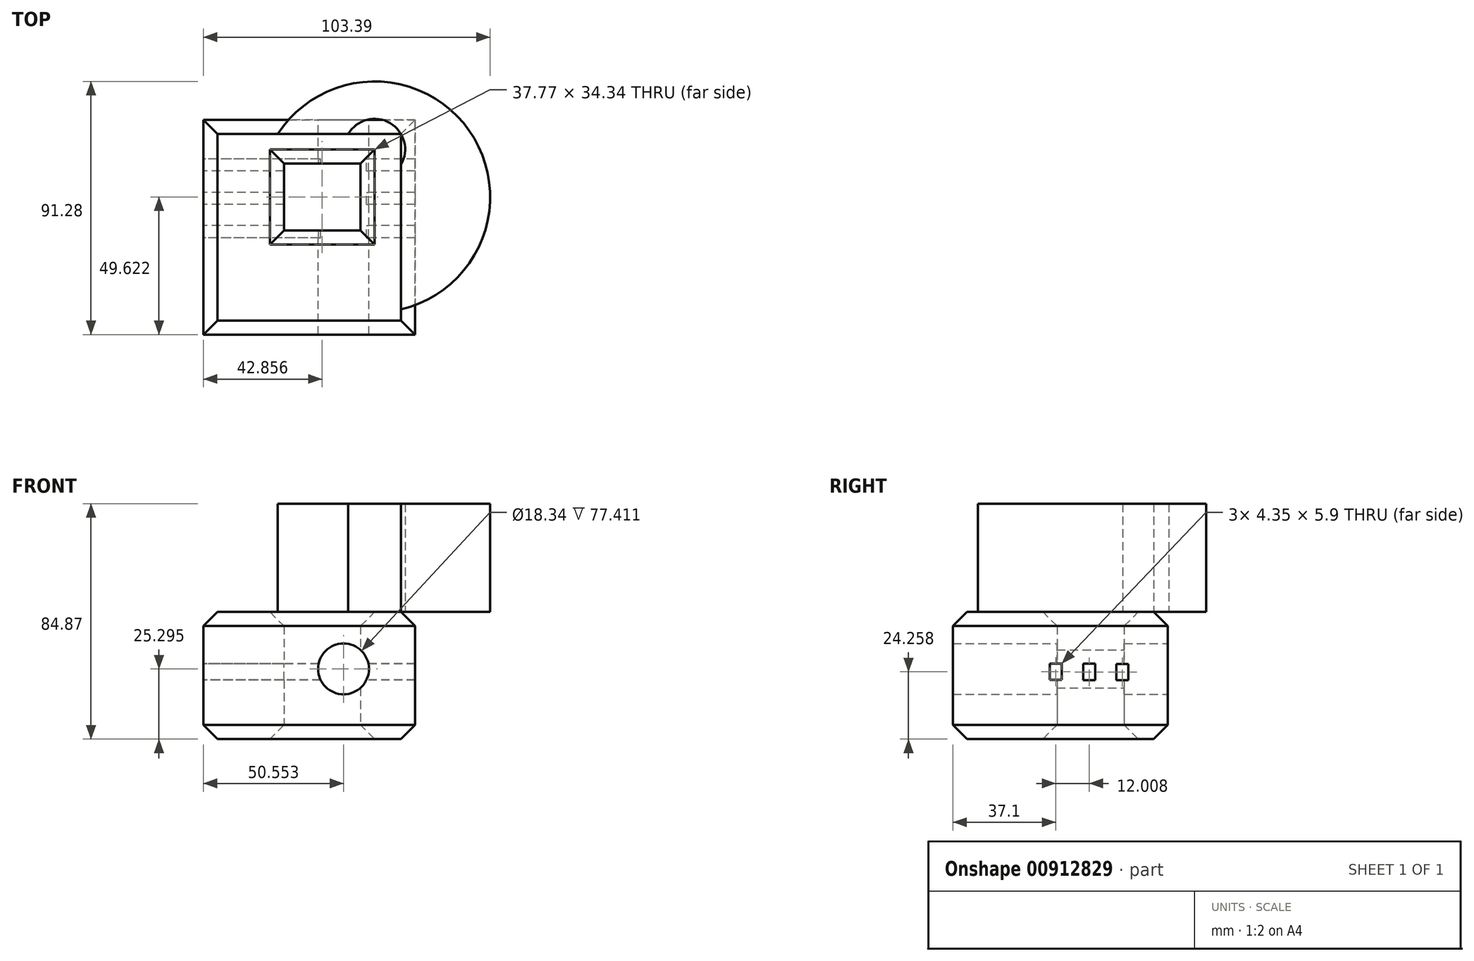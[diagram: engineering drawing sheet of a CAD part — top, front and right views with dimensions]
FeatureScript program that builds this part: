
annotation { "Feature Type Name" : "Feature", "Feature Type Description" : "" }
export const myFeature = defineFeature(function(context is Context, id is Id, definition is map)
    precondition{}
    {
        {
            var Q0;
            Q0=qCreatedBy(makeId("Top.planeOp"),FACE);
            var sketch = newSketch(context, id + "F0", { "sketchPlane" : qUnion([Q0])});
            skLineSegment(sketch, "E0.bottom", {"start": v(0, 0) * mm, "end": v(76.33, 0) * mm});
            skLineSegment(sketch, "E0.top", {"start": v(0, 77.41) * mm, "end": v(76.33, 77.41) * mm});
            skLineSegment(sketch, "E0.left", {"start": v(0, 0) * mm, "end": v(0, 77.41) * mm});
            skLineSegment(sketch, "E0.right", {"start": v(76.33, 0) * mm, "end": v(76.33, 77.41) * mm});
            skLineSegment(sketch, "E1.bottom", {"start": v(29.05, 37.53) * mm, "end": v(56.66, 37.53) * mm});
            skLineSegment(sketch, "E1.top", {"start": v(29.05, 61.71) * mm, "end": v(56.66, 61.71) * mm});
            skLineSegment(sketch, "E1.left", {"start": v(29.05, 37.53) * mm, "end": v(29.05, 61.71) * mm});
            skLineSegment(sketch, "E1.right", {"start": v(56.66, 37.53) * mm, "end": v(56.66, 61.71) * mm});
            skSolve(sketch);
        }
        {
            var Q0;
            Q0=makeQuery(id+"F0.imprint","IMPRINT",FACE,{"disambiguationData":[TD([[makeQuery(id+"F0.imprint","IMPRINT",EDGE,{"derivedFrom":sQuery(id+"F0.wireOp",EDGE,"E0.bottom")}),1.0]])]});
            extrude(context, id + "F1", {"entities" : qUnion([Q0]), "depth" : 45.83 * mm, "offsetDistance" : 25.4 * mm});
        }
        {
            var Q0;
            Q0=makeQuery(id+"F1.opExtrude","CAP_FACE",FACE,{"disambiguationData":[OSD([sQuery(id+"F0.wireOp",EDGE,"E0.bottom"),sQuery(id+"F0.wireOp",EDGE,"E0.top"),sQuery(id+"F0.wireOp",EDGE,"E0.left"),sQuery(id+"F0.wireOp",EDGE,"E0.right"),sQuery(id+"F0.wireOp",EDGE,"E1.bottom"),sQuery(id+"F0.wireOp",EDGE,"E1.top"),sQuery(id+"F0.wireOp",EDGE,"E1.left"),sQuery(id+"F0.wireOp",EDGE,"E1.right")])],"isStart":false});
            var Q1;
            Q1=makeQuery(id+"F1.opExtrude","CAP_FACE",FACE,{"disambiguationData":[OSD([sQuery(id+"F0.wireOp",EDGE,"E0.bottom"),sQuery(id+"F0.wireOp",EDGE,"E0.top"),sQuery(id+"F0.wireOp",EDGE,"E0.left"),sQuery(id+"F0.wireOp",EDGE,"E0.right"),sQuery(id+"F0.wireOp",EDGE,"E1.bottom"),sQuery(id+"F0.wireOp",EDGE,"E1.top"),sQuery(id+"F0.wireOp",EDGE,"E1.left"),sQuery(id+"F0.wireOp",EDGE,"E1.right")])],"isStart":true});
            chamfer(context, id + "F2", {"entities" : qUnion([Q0, Q1]), "width" : 5.08 * mm, "tangentPropagation" : true});
        }
        {
            var Q0;
            Q0=makeQuery(id+"F1.opExtrude","SWEPT_FACE",FACE,{"disambiguationData":[OSD([sQuery(id+"F0.wireOp",EDGE,"E0.top")])]});
            var sketch = newSketch(context, id + "F3", { "sketchPlane" : qUnion([Q0])});
            skCircle(sketch, "E2", {"center": v(-50.55, 25.3) * mm, "radius": 9.17 * mm});
            skSolve(sketch);
        }
        {
            var Q0;
            Q0=makeQuery(id+"F3.imprint","IMPRINT",FACE,{"disambiguationData":[TD([[makeQuery(id+"F3.imprint","IMPRINT",EDGE,{"derivedFrom":sQuery(id+"F3.wireOp",EDGE,"E2")}),1.0]])]});
            var Q1;
            Q1=sQuery(id+"F3.wireOp",EDGE,"E2");
            var Q2;
            Q2=makeQuery(id+"F1.opExtrude","SWEPT_FACE",FACE,{"disambiguationData":[OSD([sQuery(id+"F0.wireOp",EDGE,"E0.bottom")])]});
            extrude(context, id + "F4", {"entities" : qUnion([Q0]), "operationType" : NewBodyOperationType.REMOVE, "surfaceEntities" : qUnion([Q1]), "endBound" : BoundingType.UP_TO_SURFACE, "oppositeDirection" : true, "depth" : 25.4 * mm, "endBoundEntityFace" : qUnion([Q2]), "offsetDistance" : 25.4 * mm});
        }
        {
            var Q0;
            Q0=makeQuery(id+"F1.opExtrude","SWEPT_FACE",FACE,{"disambiguationData":[OSD([sQuery(id+"F0.wireOp",EDGE,"E0.left")])]});
            var sketch = newSketch(context, id + "F5", { "sketchPlane" : qUnion([Q0])});
            skLineSegment(sketch, "E3.bottom", {"start": v(-63.3, 21.21) * mm, "end": v(-58.94, 21.21) * mm});
            skLineSegment(sketch, "E3.top", {"start": v(-63.3, 27.1) * mm, "end": v(-58.94, 27.1) * mm});
            skLineSegment(sketch, "E3.left", {"start": v(-63.3, 21.21) * mm, "end": v(-63.3, 27.1) * mm});
            skLineSegment(sketch, "E3.right", {"start": v(-58.94, 21.21) * mm, "end": v(-58.94, 27.1) * mm});
            skLineSegment(sketch, "E4.1.0.0", {"start": v(-51.29, 21.26) * mm, "end": v(-46.93, 21.26) * mm});
            skLineSegment(sketch, "E4.1.0.1", {"start": v(-51.29, 27.16) * mm, "end": v(-46.93, 27.16) * mm});
            skLineSegment(sketch, "E4.1.0.2", {"start": v(-51.29, 21.26) * mm, "end": v(-51.29, 27.16) * mm});
            skLineSegment(sketch, "E4.1.0.3", {"start": v(-46.93, 21.26) * mm, "end": v(-46.93, 27.16) * mm});
            skLineSegment(sketch, "E4.2.0.0", {"start": v(-39.28, 21.3) * mm, "end": v(-34.92, 21.3) * mm});
            skLineSegment(sketch, "E4.2.0.1", {"start": v(-39.28, 27.2) * mm, "end": v(-34.92, 27.2) * mm});
            skLineSegment(sketch, "E4.2.0.2", {"start": v(-39.28, 21.3) * mm, "end": v(-39.28, 27.2) * mm});
            skLineSegment(sketch, "E4.2.0.3", {"start": v(-34.92, 21.3) * mm, "end": v(-34.92, 27.2) * mm});
            skLineSegment(sketch, "E4.direction1", {"start": v(-63.3, 21.21) * mm, "end": v(-51.29, 21.26) * mm, "construction": true});
            skSolve(sketch);
        }
        {
            var Q0;
            Q0 = qSketchRegion(id + "F5", true);
            extrude(context, id + "F6", {"entities" : qUnion([Q0]), "operationType" : NewBodyOperationType.REMOVE, "endBound" : BoundingType.THROUGH_ALL, "oppositeDirection" : true, "depth" : 25.4 * mm, "offsetDistance" : 25.4 * mm});
        }
        {
            var Q0;
            Q0=makeQuery(id+"F1.opExtrude","CAP_FACE",FACE,{"disambiguationData":[OSD([sQuery(id+"F0.wireOp",EDGE,"E0.bottom"),sQuery(id+"F0.wireOp",EDGE,"E0.top"),sQuery(id+"F0.wireOp",EDGE,"E0.left"),sQuery(id+"F0.wireOp",EDGE,"E0.right"),sQuery(id+"F0.wireOp",EDGE,"E1.bottom"),sQuery(id+"F0.wireOp",EDGE,"E1.top"),sQuery(id+"F0.wireOp",EDGE,"E1.left"),sQuery(id+"F0.wireOp",EDGE,"E1.right")])],"isStart":false});
            var sketch = newSketch(context, id + "F7", { "sketchPlane" : qUnion([Q0])});
            skCircle(sketch, "E5", {"center": v(61.74, 49.62) * mm, "radius": 41.65 * mm});
            skCircle(sketch, "E6", {"center": v(61.74, 66.8) * mm, "radius": 11 * mm});
            skSolve(sketch);
        }
        {
            var Q0;
            {var subQ1=sQuery(id+"F0.wireOp",EDGE,"E0.right");var subQ2=sQuery(id+"F0.wireOp",EDGE,"E0.top");var subQ3=makeQuery(id+"F1.opExtrude","CAP_FACE",FACE,{"disambiguationData":[OSD([sQuery(id+"F0.wireOp",EDGE,"E0.bottom"),subQ2,sQuery(id+"F0.wireOp",EDGE,"E0.left"),subQ1,sQuery(id+"F0.wireOp",EDGE,"E1.bottom"),sQuery(id+"F0.wireOp",EDGE,"E1.top"),sQuery(id+"F0.wireOp",EDGE,"E1.left"),sQuery(id+"F0.wireOp",EDGE,"E1.right")])],"isStart":false});var subQ4=makeQuery(id+"F2.opChamfer","BLEND_EDGE",EDGE,{"blendedFrom":[makeQuery(id+"F1.opExtrude","CAP_EDGE",EDGE,{"disambiguationData":[OSD([subQ2])],"isStart":false}),subQ3],"blendedInto":[subQ3]});var subQ6=sQuery(id+"F7.wireOp",EDGE,"E5");var subQ7=makeQuery(id+"F7.imprint","INTERSECT",VERTEX,{"derivedFrom":[subQ4,subQ6]});Q0=makeQuery(id+"F7.imprint","IMPRINT",FACE,{"disambiguationData":[TD([[makeQuery(id+"F7.imprint","IMPRINT",EDGE,{"disambiguationData":[TD([[subQ7,1.0]])],"derivedFrom":subQ6}),1.0]])]});}
            extrude(context, id + "F8", {"entities" : qUnion([Q0]), "depth" : 39.04 * mm, "offsetDistance" : 25.4 * mm});
        }
    });
